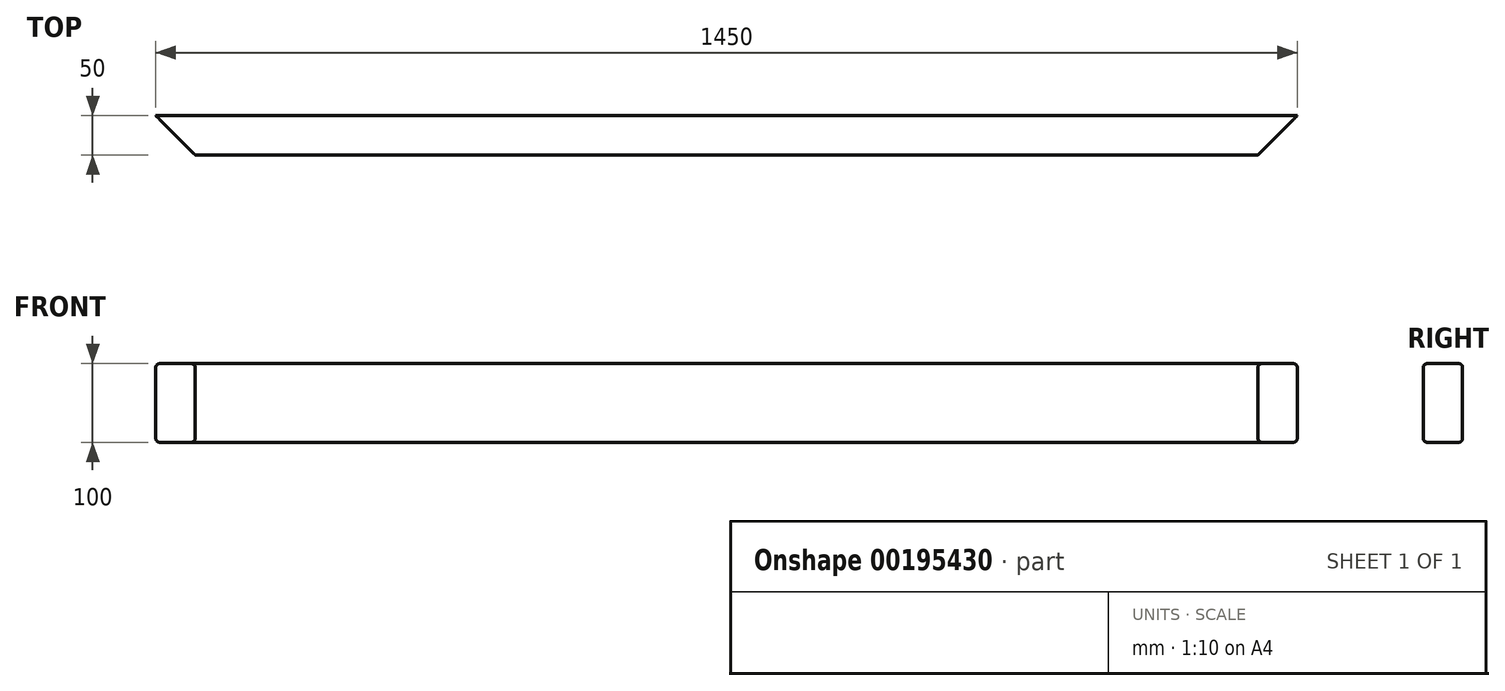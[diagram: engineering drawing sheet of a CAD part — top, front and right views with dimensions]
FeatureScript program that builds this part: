
annotation { "Feature Type Name" : "Feature", "Feature Type Description" : "" }
export const myFeature = defineFeature(function(context is Context, id is Id, definition is map)
    precondition{}
    {
        {
            var Q0;
            Q0=qCreatedBy(makeId("Front.planeOp"),FACE);
            var sketch = newSketch(context, id + "F0", { "sketchPlane" : qUnion([Q0])});
            skLineSegment(sketch, "E0.bottom", {"start": v(799.66, 0) * mm, "end": v(-650.34, 0) * mm});
            skLineSegment(sketch, "E0.top", {"start": v(799.66, 100) * mm, "end": v(-650.34, 100) * mm});
            skLineSegment(sketch, "E0.left", {"start": v(799.66, 0) * mm, "end": v(799.66, 100) * mm});
            skLineSegment(sketch, "E0.right", {"start": v(-650.34, 0) * mm, "end": v(-650.34, 100) * mm});
            skSolve(sketch);
        }
        {
            var Q0;
            Q0 = qSketchRegion(id + "F0", true);
            extrude(context, id + "F4", {"entities" : qUnion([Q0]), "depth" : 50 * mm});
        }
        {
            var Q0;
            Q0=makeQuery(id+"F4.opExtrude","CAP_EDGE",EDGE,{"disambiguationData":[OSD([sQuery(id+"F0.wireOp",EDGE,"E0.left")])],"isStart":false});
            chamfer(context, id + "F1", {"entities" : qUnion([Q0]), "width" : 50 * mm, "tangentPropagation" : true});
        }
        {
            var Q0;
            Q0=makeQuery(id+"F4.opExtrude","CAP_EDGE",EDGE,{"disambiguationData":[OSD([sQuery(id+"F0.wireOp",EDGE,"E0.right")])],"isStart":false});
            chamfer(context, id + "F2", {"entities" : qUnion([Q0]), "width" : 50 * mm, "tangentPropagation" : true});
        }
        {
            var Q0;
            Q0=makeQuery(id+"F4.opExtrude","CAP_EDGE",EDGE,{"disambiguationData":[OSD([sQuery(id+"F0.wireOp",EDGE,"E0.top")])],"isStart":false});
            var Q1;
            Q1=makeQuery(id+"F4.opExtrude","CAP_EDGE",EDGE,{"disambiguationData":[OSD([sQuery(id+"F0.wireOp",EDGE,"E0.bottom")])],"isStart":false});
            var Q2;
            Q2=makeQuery(id+"F4.opExtrude","CAP_EDGE",EDGE,{"disambiguationData":[OSD([sQuery(id+"F0.wireOp",EDGE,"E0.top")])],"isStart":true});
            var Q3;
            Q3=makeQuery(id+"F4.opExtrude","CAP_EDGE",EDGE,{"disambiguationData":[OSD([sQuery(id+"F0.wireOp",EDGE,"E0.bottom")])],"isStart":true});
            fillet(context, id + "F3", {"entities" : qUnion([Q0, Q1, Q2, Q3]), "radius" : 5 * mm, "tangentPropagation" : true, "allowEdgeOverflow" : false});
        }
    });
